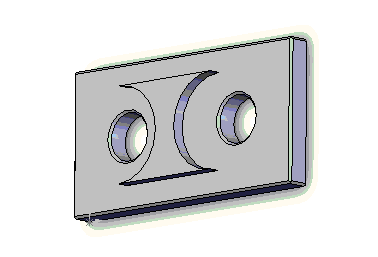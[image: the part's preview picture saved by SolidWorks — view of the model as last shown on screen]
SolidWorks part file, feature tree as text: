
SOLIDWORKS PART (.sldprt)
format: sldprt  version: not decoded by parser v0  size: 152,064 bytes
history: native  units: mm
features: chamfer x3, sketch x2, extrude x2, material x1 (+11 scaffold rows collapsed)
feature tree (19):
  scaffold x11  (default folders/planes/origin — collapsed)
  material  "Materiál <není určen>"
  sketch  "Skica1"  dims[D1=30.0mm D2=60.0mm D3=30.0mm D4=120.0mm D5=60.0mm]
  extrude  "Vysunout1"  Depth=10mm
  chamfer  "Zkosit1"  Distance=1mm Angle=45deg
  chamfer  "Zkosit2"  Distance=1mm Angle=45deg
  chamfer  "Zkosit3"  Distance=1mm Angle=45deg
  sketch  "Skica2"
  extrude  "Vysunout2"  Depth=5mm
decode coverage: 6 of 7 modeling features carry decoded parameters
note: suppression state not decoded; provenance and decode notes live in map.json
